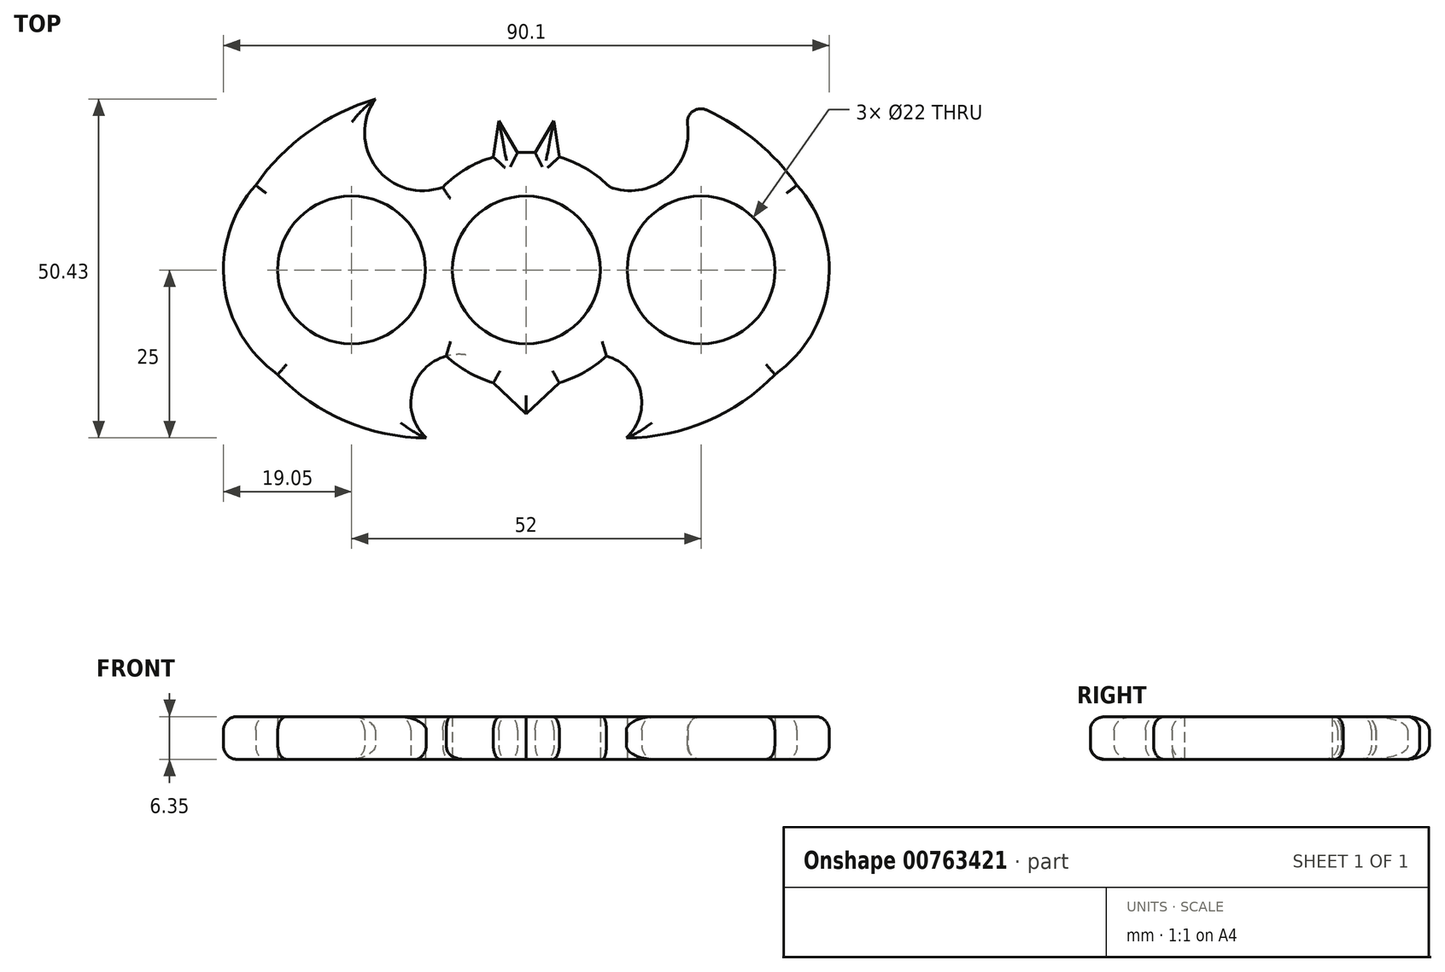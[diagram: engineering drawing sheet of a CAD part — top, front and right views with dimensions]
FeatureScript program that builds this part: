
annotation { "Feature Type Name" : "Feature", "Feature Type Description" : "" }
export const myFeature = defineFeature(function(context is Context, id is Id, definition is map)
    precondition{}
    {
        {
            var Q0;
            Q0=qCreatedBy(makeId("Top.planeOp"),FACE);
            var sketch = newSketch(context, id + "F0", { "sketchPlane" : qUnion([Q0])});
            skCircle(sketch, "E0", {"center": v(0, 0) * mm, "radius": 11 * mm});
            skCircle(sketch, "E1", {"center": v(0, 0) * mm, "radius": 17.5 * mm});
            skLineSegment(sketch, "E2", {"start": v(0, 0) * mm, "end": v(-26, 0) * mm});
            skCircle(sketch, "E3", {"center": v(-26, 0) * mm, "radius": 11 * mm});
            skLineSegment(sketch, "E4", {"start": v(0, 0) * mm, "end": v(26, 0) * mm});
            skCircle(sketch, "E5", {"center": v(26, 0) * mm, "radius": 11 * mm});
            skArc(sketch, "E6", {"start": v(36.96, -15.58) * mm, "mid": v(44.92, -2.21) * mm, "end": v(40.26, 12.63) * mm});
            skArc(sketch, "E7", {"start": v(-22.47, 25.43) * mm, "mid": v(-32.44, 20.53) * mm, "end": v(-40.26, 12.63) * mm});
            skArc(sketch, "E8", {"start": v(-22.47, 25.43) * mm, "mid": v(-22.28, 15.18) * mm, "end": v(-12.43, 12.31) * mm});
            skArc(sketch, "E9.trimOffspring", {"start": v(-40.26, 12.63) * mm, "mid": v(-44.92, -2.21) * mm, "end": v(-36.96, -15.58) * mm});
            skArc(sketch, "E10.MirrorCS", {"start": v(22.47, 25.43) * mm, "mid": v(22.28, 15.18) * mm, "end": v(12.43, 12.31) * mm});
            skArc(sketch, "E11.MirrorCS", {"start": v(22.47, 25.43) * mm, "mid": v(32.44, 20.53) * mm, "end": v(40.26, 12.63) * mm});
            skArc(sketch, "E12", {"start": v(-36.96, -15.58) * mm, "mid": v(-26.87, -22.53) * mm, "end": v(-14.87, -25) * mm});
            skArc(sketch, "E13", {"start": v(-11.9, -12.82) * mm, "mid": v(-16.97, -18.04) * mm, "end": v(-14.87, -25) * mm});
            skArc(sketch, "E14.MirrorCS", {"start": v(11.9, -12.82) * mm, "mid": v(16.97, -18.04) * mm, "end": v(14.87, -25) * mm});
            skArc(sketch, "E15.MirrorCS", {"start": v(36.96, -15.58) * mm, "mid": v(26.87, -22.53) * mm, "end": v(14.87, -25) * mm});
            skPoint(sketch, "E16.end.orphan", {"position": v(2.34, 18.82) * mm});
            skPoint(sketch, "E17.orphan", {"position": v(4.9, 16.8) * mm});
            skPoint(sketch, "E18.end.orphan", {"position": v(-1.3, 17.45) * mm});
            skPoint(sketch, "E19.end.orphan", {"position": v(-2.23, 18.82) * mm});
            skPoint(sketch, "E20.MirrorCS.end.orphan", {"position": v(1.3, 17.45) * mm});
            skPoint(sketch, "E20.MirrorCS.start.orphan", {"position": v(2.23, 18.82) * mm});
            skPoint(sketch, "E21.end.orphan", {"position": v(-4.8, 18.35) * mm});
            skPoint(sketch, "E22.MirrorCS.end.orphan", {"position": v(4.8, 18.35) * mm});
            skLineSegment(sketch, "E23", {"start": v(-1.3, 17.45) * mm, "end": v(-4.1, 22.22) * mm});
            skLineSegment(sketch, "E24", {"start": v(-4.1, 22.22) * mm, "end": v(-4.9, 16.8) * mm});
            skLineSegment(sketch, "E25.MirrorCS", {"start": v(1.3, 17.45) * mm, "end": v(4.1, 22.22) * mm});
            skLineSegment(sketch, "E26.MirrorCS", {"start": v(4.1, 22.22) * mm, "end": v(4.9, 16.8) * mm});
            skPoint(sketch, "E27.end.orphan", {"position": v(0, -21.45) * mm});
            skPoint(sketch, "E27.start.orphan", {"position": v(-5.02, -16.76) * mm});
            skPoint(sketch, "E28.MirrorCS.start.orphan", {"position": v(5.02, -16.76) * mm});
            skPoint(sketch, "E29.MirrorCS.end.orphan", {"position": v(-4.9, -16.8) * mm});
            skPoint(sketch, "E29.MirrorCS.start.orphan", {"position": v(-4.1, -22.22) * mm});
            skLineSegment(sketch, "E30", {"start": v(-4.9, -16.8) * mm, "end": v(0, -21.45) * mm});
            skLineSegment(sketch, "E31.MirrorCS", {"start": v(4.9, -16.8) * mm, "end": v(0, -21.45) * mm});
            skSolve(sketch);
        }
        {
            var Q0;
            Q0=qSketchRegion(id+"F0",true);
            extrude(context, id + "F1", {"entities" : qUnion([Q0]), "depth" : 6.35 * mm, "offsetDistance" : 25.4 * mm});
        }
        {
            var Q0;
            Q0=makeQuery(id+"F1.opExtrude","CAP_EDGE",EDGE,{"disambiguationData":[OSD([sQuery(id+"F0.wireOp",EDGE,"E7")])],"isStart":false});
            var Q1;
            Q1=makeQuery(id+"F1.opExtrude","CAP_EDGE",EDGE,{"disambiguationData":[OSD([sQuery(id+"F0.wireOp",EDGE,"E9.trimOffspring")])],"isStart":false});
            var Q2;
            Q2=makeQuery(id+"F1.opExtrude","CAP_EDGE",EDGE,{"disambiguationData":[OSD([sQuery(id+"F0.wireOp",EDGE,"E12")])],"isStart":false});
            var Q3;
            Q3=makeQuery(id+"F1.opExtrude","CAP_EDGE",EDGE,{"disambiguationData":[OSD([sQuery(id+"F0.wireOp",EDGE,"E13")])],"isStart":false});
            var Q4;
            {var subQ0=sQuery(id+"F0.wireOp",EDGE,"E1");Q4=makeQuery(id+"F1.opExtrude","CAP_EDGE",EDGE,{"disambiguationData":[OSD([subQ0]),TDD([makeQuery(id+"F0.imprint","IMPRINT",EDGE,{"disambiguationData":[TD([[makeQuery(id+"F0.imprint","INTERSECT",VERTEX,{"derivedFrom":[subQ0,sQuery(id+"F0.wireOp",EDGE,"E13")]}),-1.0]])],"derivedFrom":subQ0})])],"isStart":false});}
            var Q5;
            Q5=makeQuery(id+"F1.opExtrude","CAP_EDGE",EDGE,{"disambiguationData":[OSD([sQuery(id+"F0.wireOp",EDGE,"E30")])],"isStart":false});
            var Q6;
            Q6=makeQuery(id+"F1.opExtrude","CAP_EDGE",EDGE,{"disambiguationData":[OSD([sQuery(id+"F0.wireOp",EDGE,"E31.MirrorCS")])],"isStart":true});
            var Q7;
            {var subQ0=sQuery(id+"F0.wireOp",EDGE,"E1");Q7=makeQuery(id+"F1.opExtrude","CAP_EDGE",EDGE,{"disambiguationData":[OSD([subQ0]),TDD([makeQuery(id+"F0.imprint","IMPRINT",EDGE,{"disambiguationData":[TD([[makeQuery(id+"F0.imprint","INTERSECT",VERTEX,{"derivedFrom":[subQ0,sQuery(id+"F0.wireOp",EDGE,"E14.MirrorCS")]}),1.0]])],"derivedFrom":subQ0})])],"isStart":false});}
            var Q8;
            Q8=makeQuery(id+"F1.opExtrude","CAP_EDGE",EDGE,{"disambiguationData":[OSD([sQuery(id+"F0.wireOp",EDGE,"E14.MirrorCS")])],"isStart":false});
            var Q9;
            Q9=makeQuery(id+"F1.opExtrude","CAP_EDGE",EDGE,{"disambiguationData":[OSD([sQuery(id+"F0.wireOp",EDGE,"E15.MirrorCS")])],"isStart":false});
            var Q10;
            Q10=makeQuery(id+"F1.opExtrude","CAP_EDGE",EDGE,{"disambiguationData":[OSD([sQuery(id+"F0.wireOp",EDGE,"E6")])],"isStart":false});
            var Q11;
            Q11=makeQuery(id+"F1.opExtrude","CAP_EDGE",EDGE,{"disambiguationData":[OSD([sQuery(id+"F0.wireOp",EDGE,"E11.MirrorCS")])],"isStart":false});
            var Q12;
            Q12=makeQuery(id+"F1.opExtrude","CAP_EDGE",EDGE,{"disambiguationData":[OSD([sQuery(id+"F0.wireOp",EDGE,"E10.MirrorCS")])],"isStart":false});
            var Q13;
            {var subQ0=sQuery(id+"F0.wireOp",EDGE,"E1");Q13=makeQuery(id+"F1.opExtrude","CAP_EDGE",EDGE,{"disambiguationData":[OSD([subQ0]),TDD([makeQuery(id+"F0.imprint","IMPRINT",EDGE,{"disambiguationData":[TD([[makeQuery(id+"F0.imprint","INTERSECT",VERTEX,{"derivedFrom":[subQ0,sQuery(id+"F0.wireOp",EDGE,"E10.MirrorCS")]}),-1.0]])],"derivedFrom":subQ0})])],"isStart":false});}
            var Q14;
            Q14=makeQuery(id+"F1.opExtrude","CAP_EDGE",EDGE,{"disambiguationData":[OSD([sQuery(id+"F0.wireOp",EDGE,"E26.MirrorCS")])],"isStart":false});
            var Q15;
            Q15=makeQuery(id+"F1.opExtrude","CAP_EDGE",EDGE,{"disambiguationData":[OSD([sQuery(id+"F0.wireOp",EDGE,"E23")])],"isStart":false});
            var Q16;
            Q16=makeQuery(id+"F1.opExtrude","CAP_EDGE",EDGE,{"disambiguationData":[OSD([sQuery(id+"F0.wireOp",EDGE,"E8")])],"isStart":false});
            var Q17;
            {var subQ0=sQuery(id+"F0.wireOp",EDGE,"E1");Q17=makeQuery(id+"F1.opExtrude","CAP_EDGE",EDGE,{"disambiguationData":[OSD([subQ0]),TDD([makeQuery(id+"F0.imprint","IMPRINT",EDGE,{"disambiguationData":[TD([[makeQuery(id+"F0.imprint","INTERSECT",VERTEX,{"derivedFrom":[subQ0,sQuery(id+"F0.wireOp",EDGE,"E8")]}),1.0]])],"derivedFrom":subQ0})])],"isStart":false});}
            var Q18;
            Q18=makeQuery(id+"F1.opExtrude","CAP_EDGE",EDGE,{"disambiguationData":[OSD([sQuery(id+"F0.wireOp",EDGE,"E24")])],"isStart":false});
            var Q19;
            Q19=makeQuery(id+"F1.opExtrude","CAP_EDGE",EDGE,{"disambiguationData":[OSD([sQuery(id+"F0.wireOp",EDGE,"E25.MirrorCS")])],"isStart":false});
            var Q20;
            Q20=makeQuery(id+"F1.opExtrude","CAP_EDGE",EDGE,{"disambiguationData":[OSD([sQuery(id+"F0.wireOp",EDGE,"E31.MirrorCS")])],"isStart":false});
            var Q21;
            Q21=makeQuery(id+"F1.opExtrude","SWEPT_EDGE",EDGE,{"disambiguationData":[OSD([sQuery(id+"F0.wireOp",EDGE,"E10.MirrorCS"),sQuery(id+"F0.wireOp",EDGE,"E11.MirrorCS")])]});
            var Q22;
            Q22=makeQuery(id+"F1.opExtrude","CAP_EDGE",EDGE,{"disambiguationData":[OSD([sQuery(id+"F0.wireOp",EDGE,"E11.MirrorCS")])],"isStart":true});
            var Q23;
            Q23=makeQuery(id+"F1.opExtrude","CAP_EDGE",EDGE,{"disambiguationData":[OSD([sQuery(id+"F0.wireOp",EDGE,"E6")])],"isStart":true});
            var Q24;
            Q24=makeQuery(id+"F1.opExtrude","CAP_EDGE",EDGE,{"disambiguationData":[OSD([sQuery(id+"F0.wireOp",EDGE,"E15.MirrorCS")])],"isStart":true});
            var Q25;
            Q25=makeQuery(id+"F1.opExtrude","CAP_EDGE",EDGE,{"disambiguationData":[OSD([sQuery(id+"F0.wireOp",EDGE,"E14.MirrorCS")])],"isStart":true});
            var Q26;
            {var subQ0=sQuery(id+"F0.wireOp",EDGE,"E1");Q26=makeQuery(id+"F1.opExtrude","CAP_EDGE",EDGE,{"disambiguationData":[OSD([subQ0]),TDD([makeQuery(id+"F0.imprint","IMPRINT",EDGE,{"disambiguationData":[TD([[makeQuery(id+"F0.imprint","INTERSECT",VERTEX,{"derivedFrom":[subQ0,sQuery(id+"F0.wireOp",EDGE,"E14.MirrorCS")]}),1.0]])],"derivedFrom":subQ0})])],"isStart":true});}
            var Q27;
            Q27=makeQuery(id+"F1.opExtrude","CAP_EDGE",EDGE,{"disambiguationData":[OSD([sQuery(id+"F0.wireOp",EDGE,"E30")])],"isStart":true});
            var Q28;
            {var subQ0=sQuery(id+"F0.wireOp",EDGE,"E1");Q28=makeQuery(id+"F1.opExtrude","CAP_EDGE",EDGE,{"disambiguationData":[OSD([subQ0]),TDD([makeQuery(id+"F0.imprint","IMPRINT",EDGE,{"disambiguationData":[TD([[makeQuery(id+"F0.imprint","INTERSECT",VERTEX,{"derivedFrom":[subQ0,sQuery(id+"F0.wireOp",EDGE,"E13")]}),-1.0]])],"derivedFrom":subQ0})])],"isStart":true});}
            var Q29;
            Q29=makeQuery(id+"F1.opExtrude","CAP_EDGE",EDGE,{"disambiguationData":[OSD([sQuery(id+"F0.wireOp",EDGE,"E12")])],"isStart":true});
            var Q30;
            Q30=makeQuery(id+"F1.opExtrude","CAP_EDGE",EDGE,{"disambiguationData":[OSD([sQuery(id+"F0.wireOp",EDGE,"E9.trimOffspring")])],"isStart":true});
            var Q31;
            Q31=makeQuery(id+"F1.opExtrude","CAP_EDGE",EDGE,{"disambiguationData":[OSD([sQuery(id+"F0.wireOp",EDGE,"E7")])],"isStart":true});
            var Q32;
            Q32=makeQuery(id+"F1.opExtrude","CAP_EDGE",EDGE,{"disambiguationData":[OSD([sQuery(id+"F0.wireOp",EDGE,"E8")])],"isStart":true});
            var Q33;
            {var subQ0=sQuery(id+"F0.wireOp",EDGE,"E1");Q33=makeQuery(id+"F1.opExtrude","CAP_EDGE",EDGE,{"disambiguationData":[OSD([subQ0]),TDD([makeQuery(id+"F0.imprint","IMPRINT",EDGE,{"disambiguationData":[TD([[makeQuery(id+"F0.imprint","INTERSECT",VERTEX,{"derivedFrom":[subQ0,sQuery(id+"F0.wireOp",EDGE,"E8")]}),1.0]])],"derivedFrom":subQ0})])],"isStart":true});}
            var Q34;
            Q34=makeQuery(id+"F1.opExtrude","CAP_EDGE",EDGE,{"disambiguationData":[OSD([sQuery(id+"F0.wireOp",EDGE,"E24")])],"isStart":true});
            var Q35;
            Q35=makeQuery(id+"F1.opExtrude","CAP_EDGE",EDGE,{"disambiguationData":[OSD([sQuery(id+"F0.wireOp",EDGE,"E25.MirrorCS")])],"isStart":true});
            var Q36;
            {var subQ0=sQuery(id+"F0.wireOp",EDGE,"E1");Q36=makeQuery(id+"F1.opExtrude","CAP_EDGE",EDGE,{"disambiguationData":[OSD([subQ0]),TDD([makeQuery(id+"F0.imprint","IMPRINT",EDGE,{"disambiguationData":[TD([[makeQuery(id+"F0.imprint","INTERSECT",VERTEX,{"derivedFrom":[subQ0,sQuery(id+"F0.wireOp",EDGE,"E10.MirrorCS")]}),-1.0]])],"derivedFrom":subQ0})])],"isStart":true});}
            var Q37;
            Q37=makeQuery(id+"F1.opExtrude","CAP_EDGE",EDGE,{"disambiguationData":[OSD([sQuery(id+"F0.wireOp",EDGE,"E26.MirrorCS")])],"isStart":true});
            var Q38;
            Q38=makeQuery(id+"F1.opExtrude","CAP_EDGE",EDGE,{"disambiguationData":[OSD([sQuery(id+"F0.wireOp",EDGE,"E23")])],"isStart":true});
            var Q39;
            {var subQ0=sQuery(id+"F0.wireOp",EDGE,"E1");Q39=makeQuery(id+"F1.opExtrude","CAP_EDGE",EDGE,{"disambiguationData":[OSD([subQ0]),TDD([makeQuery(id+"F0.imprint","IMPRINT",EDGE,{"disambiguationData":[TD([[makeQuery(id+"F0.imprint","INTERSECT",VERTEX,{"derivedFrom":[subQ0,sQuery(id+"F0.wireOp",EDGE,"E23")]}),1.0]])],"derivedFrom":subQ0})])],"isStart":true});}
            var Q40;
            Q40=makeQuery(id+"F1.opExtrude","SWEPT_FACE",FACE,{"disambiguationData":[OSD([sQuery(id+"F0.wireOp",EDGE,"E10.MirrorCS")])]});
            var Q41;
            {var subQ0=sQuery(id+"F0.wireOp",EDGE,"E1");Q41=makeQuery(id+"F1.opExtrude","CAP_EDGE",EDGE,{"disambiguationData":[OSD([subQ0]),TDD([makeQuery(id+"F0.imprint","IMPRINT",EDGE,{"disambiguationData":[TD([[makeQuery(id+"F0.imprint","INTERSECT",VERTEX,{"derivedFrom":[subQ0,sQuery(id+"F0.wireOp",EDGE,"E23")]}),1.0]])],"derivedFrom":subQ0})])],"isStart":false});}
            fillet(context, id + "F2", {"entities" : qUnion([Q0, Q1, Q2, Q3, Q4, Q5, Q6, Q7, Q8, Q9, Q10, Q11, Q12, Q13, Q14, Q15, Q16, Q17, Q18, Q19, Q20, Q21, Q22, Q23, Q24, Q25, Q26, Q27, Q28, Q29, Q30, Q31, Q32, Q33, Q34, Q35, Q36, Q37, Q38, Q39, Q40, Q41]), "radius" : 2 * mm, "tangentPropagation" : true, "allowEdgeOverflow" : false});
        }
    });
